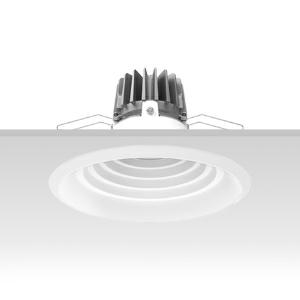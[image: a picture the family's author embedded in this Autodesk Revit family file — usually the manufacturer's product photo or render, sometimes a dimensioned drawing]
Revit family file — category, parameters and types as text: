
# Revit family: 3f_filippi_-_3f_reno_bianco_ellittico_3f_filippi_-_30785_-_3f_reno_200_wh_2000-840_ell
name_source: partatom
category: Lighting Fixtures
units: mm (PartAtom-declared; Revit-internal decimal feet)

## family parameters
Cut with Voids When Loaded = No
Host = Face
Light Source = No
Part Type = Normal
Room Calculation Point = No
Round Connector Dimension = Use Diameter
Shared = No

## types (1)
- 3F Filippi - 3F Reno Bianco Ellittico (1 x LED, 2093 lm, 20 W, 4000 K)
    Apparent Load = 20 VA
    Approval mark = CE
    CIE Flux Codes = 77 98 100 100 100
    Color Rendering = 80
    Color Temperature = 4000 K
    Control Gear = Electronic ballast
    Default Elevation = 1800 mm
    Description = ILLUMINOTECHNICAL
Luminous efficiency 100% (DLOR 100%, ULOR 0%).
Initial luminous flux of the luminaire 2093 lm.
Direct symmetric elliptical distribution.
Installation Interdistance Transv.D = 0.79 x hu - Long.D = 1.49 x hu.
Tabular UGR (CIE 117 - 4H-8H; S=0.25H; 70/50/20): RUG 17.3 - 21.8.
Beam angle: 65° - 93°.
Luminous efficacy 105 lm/W.
Lifetime (L90/B10): 30000 h. (tq+25°C)
Lifetime (L85/B10): 50000 h. (tq+25°C)
Lifetime (L70/B10): 80000 h. (tq+25°C)
Sudden decreased luminous flux after 50000 hours: 0% (C0).
Photobiological safety in compliance with IEC/TR 62778: RG1 low risk, (IEC 62471).
In compliance with IEC/EN 62722-2-1 - IEC/EN 62717 standards.

SOURCE
Compact LED module 2000/840.
Energy efficiency class (UE 2019/2020 - UE 2019/2015): D.
CIE 13.3 Colour rendering index: CRI >80 (R9 <50%).
IES TM-30 Fidelity Index: Rf = 84 Rg = 95.
CCT nominal colour temperature 4000 K.
Colour initial tolerance (MacAdam): SDCM 3.
Zhaga Book 3 compliant.

MECHANICAL
Passive heat dissipator in die-casting aluminium, oversized, for optimum thermal management of the LED module.
Parabolic element with graduated/concentric rings in white polycarbonate.
Internal specular metallic louvre to optimise control of the luminous flux in polycarbonate.
Transparent external lens with glossy and satin differentiated surfaces, with a cooling and anti-insect system in methacrylate (PMMA).
Fastening spring clips in stainless steel.
Dimensions: diameter 216 mm, height 142 mm. Weight 0.81 kg.
IP44 protection degree for exposed part, IP20 for recessed part.
Mechanical strength to impacts IK04 (0.5 joule).
Glow-wire test resistance 650°C.

ELECTRICAL
Wiring on a separate unit.
Halogen Free electronic wiring 230V-50/60Hz, power factor 0.95, THD <25%, constant output current, SELV, class II, 1 driver.
Power of the luminaire 20 W.
ENEC - CE.
SAFE FLICKER: PstLM=<1 and SVM=<0.4 (IEC TR 61547-1 and IEC TR 63158), to ensure a more comfortable and safe light.
Luminaire compliant with EN 60598-2-22 for power supply from a centralised emergency system CPSS (Central Power Supply System), not incorporated in the luminaire - high risk areas excluded. The default power and flux are 100% in AC and 100% in DC.
Ambient temperature from 0°C to +25°C.
Temperature class T6 max 85°C.
Relative humidity UR: <85%.

INSTALLATION
Pull-up recessed fitting.
False ceiling carving: 200 mm.
All accessories dedicated to this product are available on the Catalog and on our website www.3F-Filippi.com.

APPLICATIONS
Environments: architectural, commercial, exhibition areas, transit areas, corridors, shops, display windows, service areas.
In false ceilings with narrow voids.

WARNING
Luminaire designed for disposal/recycling at end-of-life.
Replaceable (LED only) light source by a professional. Replaceable control gear by a professional.
    Height = 0 mm  [stored 0 ft]
    Lamp = 1 x LED
    Lamp Light Flux = 2093 lm
    Lamp Power = 20 W
    Lamp count = 1
    Length = 216 mm
    Lifetime = 50000 h
    Luminous efficacy = 105 lm/W
    Manufacturer = 3F Filippi
    ModVariant = No
    Model = 3F Filippi - 30785 - 3F Reno 200 WH 2000-840 ELL
    Mounting Place = Ceiling
    Mounting Type = Recessed
    Number of Poles = 1
    OnlyDefault = Yes
    Power Factor = 1
    Product Name = 3F Filippi - 3F Reno Bianco Ellittico
    Product group = recessed luminaire
    ProductGroupID = 4
    Protection Class = Protection class II
    Protection Degree = IP 20
    RLX_Detail_Level = 1
    RLX_Emergency_Light_Flux = 0 lm
    RLX_Emergency_Type = 0
    RLX_Emergency_Type_DB = No
    RlxData = <blob elided: 89001 chars, md5=110a2b05>
    Socket = socket
    Standby Power = 0 W
    System Light Flux = 2093 lm
    System Power = 20 W
    Type Comments = Product without accessories
    Type Image = 3ffilippi_3f_reno_200_wh_2000.jpg
    URL = http://relux.com
    VarID = ---
    Voltage = 0 V
    Weight = 0.00 kg
    Width = 0 mm  [stored 0 ft]

note: [stored X ft] marks values corroborated as IEEE doubles in the binary element streams (Revit-internal decimal feet)

## geometry (parser evidence)
native form markers: Blend x4, Sweep x11
no freeform markers — native parametric forms only
